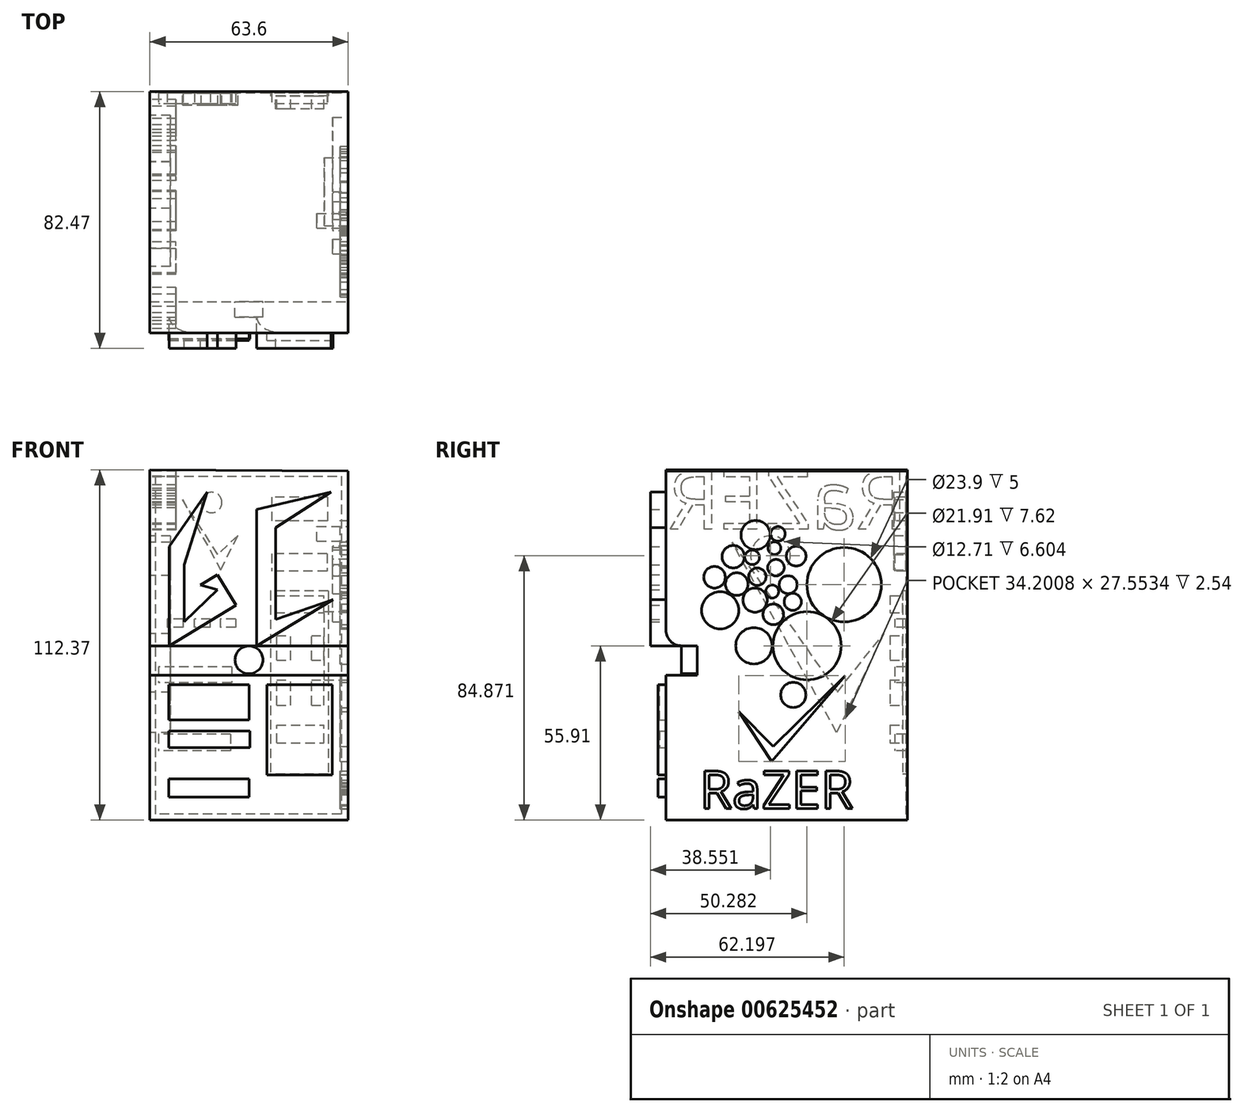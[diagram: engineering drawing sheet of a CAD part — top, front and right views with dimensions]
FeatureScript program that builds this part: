
annotation { "Feature Type Name" : "Feature", "Feature Type Description" : "" }
export const myFeature = defineFeature(function(context is Context, id is Id, definition is map)
    precondition{}
    {
        {
            var Q0;
            Q0=qCreatedBy(makeId("Front.planeOp"),FACE);
            var sketch = newSketch(context, id + "F0", { "sketchPlane" : qUnion([Q0])});
            skLineSegment(sketch, "E0", {"start": v(-45.18, 56.46) * mm, "end": v(-45.18, -55.9) * mm});
            skLineSegment(sketch, "E1", {"start": v(-45.18, -55.9) * mm, "end": v(18.42, -55.9) * mm});
            skLineSegment(sketch, "E2", {"start": v(18.42, -55.9) * mm, "end": v(18.42, 56.09) * mm});
            skLineSegment(sketch, "E3", {"start": v(18.42, 56.09) * mm, "end": v(-45.18, 56.46) * mm});
            skPoint(sketch, "E4.orphan", {"position": v(-43.53, 53.16) * mm});
            skPoint(sketch, "E5.start.orphan", {"position": v(-43.53, 51.7) * mm});
            skSolve(sketch);
        }
        {
            var Q0;
            Q0 = qSketchRegion(id + "F0", true);
            extrude(context, id + "F1", {"entities" : qUnion([Q0]), "depth" : 77.47 * mm, "offsetDistance" : 25.4 * mm});
        }
        {
            var Q0;
            Q0=makeQuery(id+"F1.opExtrude","CAP_FACE",FACE,{"disambiguationData":[OSD([sQuery(id+"F0.wireOp",EDGE,"E0"),sQuery(id+"F0.wireOp",EDGE,"E1"),sQuery(id+"F0.wireOp",EDGE,"E2"),sQuery(id+"F0.wireOp",EDGE,"E3")])],"isStart":false});
            var sketch = newSketch(context, id + "F2", { "sketchPlane" : qUnion([Q0])});
            skLineSegment(sketch, "E6", {"start": v(-26.85, 49.3) * mm, "end": v(-38.95, 31.9) * mm});
            skLineSegment(sketch, "E7", {"start": v(-38.95, 31.9) * mm, "end": v(-38.95, 0) * mm});
            skLineSegment(sketch, "E8", {"start": v(-38.95, 0) * mm, "end": v(-17.5, 13.01) * mm});
            skLineSegment(sketch, "E9", {"start": v(-17.5, 13.01) * mm, "end": v(-23.49, 22.87) * mm});
            skLineSegment(sketch, "E10", {"start": v(-23.49, 22.87) * mm, "end": v(-28.95, 19.56) * mm});
            skLineSegment(sketch, "E11", {"start": v(-28.95, 19.56) * mm, "end": v(-23.49, 17.96) * mm});
            skLineSegment(sketch, "E12", {"start": v(-23.49, 17.96) * mm, "end": v(-34.19, 7.7) * mm});
            skLineSegment(sketch, "E13", {"start": v(-34.19, 7.7) * mm, "end": v(-34.19, 26.03) * mm});
            skLineSegment(sketch, "E14", {"start": v(-34.19, 26.03) * mm, "end": v(-26.85, 49.3) * mm});
            skLineSegment(sketch, "E15", {"start": v(12.92, 49.3) * mm, "end": v(-10.9, 43.8) * mm});
            skLineSegment(sketch, "E16", {"start": v(-10.9, 43.8) * mm, "end": v(-10.9, 0) * mm});
            skLineSegment(sketch, "E17", {"start": v(-10.9, 0) * mm, "end": v(13.57, 14.85) * mm});
            skLineSegment(sketch, "E18", {"start": v(13.57, 14.85) * mm, "end": v(-4.86, 8.43) * mm});
            skLineSegment(sketch, "E19", {"start": v(-4.86, 8.43) * mm, "end": v(-4.86, 37.94) * mm});
            skLineSegment(sketch, "E20", {"start": v(-4.86, 37.94) * mm, "end": v(12.92, 49.3) * mm});
            skSolve(sketch);
        }
        {
            var Q0;
            Q0 = qSketchRegion(id + "F2", true);
            extrude(context, id + "F3", {"entities" : qUnion([Q0]), "operationType" : NewBodyOperationType.ADD, "depth" : 5 * mm, "offsetDistance" : 25.4 * mm});
        }
        {
            var Q0;
            Q0=makeQuery(id+"F1.opExtrude","CAP_FACE",FACE,{"disambiguationData":[OSD([sQuery(id+"F0.wireOp",EDGE,"E0"),sQuery(id+"F0.wireOp",EDGE,"E1"),sQuery(id+"F0.wireOp",EDGE,"E2"),sQuery(id+"F0.wireOp",EDGE,"E3")])],"isStart":false});
            var sketch = newSketch(context, id + "F4", { "sketchPlane" : qUnion([Q0])});
            skLineSegment(sketch, "E21", {"start": v(-39.13, -12.46) * mm, "end": v(-13.29, -12.46) * mm});
            skLineSegment(sketch, "E22", {"start": v(-13.29, -12.46) * mm, "end": v(-13.29, -23.83) * mm});
            skLineSegment(sketch, "E23", {"start": v(-13.29, -23.83) * mm, "end": v(-39.13, -23.83) * mm});
            skLineSegment(sketch, "E24", {"start": v(-39.13, -23.83) * mm, "end": v(-39.13, -12.46) * mm});
            skLineSegment(sketch, "E25", {"start": v(-13.1, -27.31) * mm, "end": v(-13.1, -32.63) * mm});
            skLineSegment(sketch, "E26", {"start": v(-13.1, -32.63) * mm, "end": v(-39.13, -32.63) * mm});
            skLineSegment(sketch, "E27", {"start": v(-39.13, -32.63) * mm, "end": v(-39.13, -27.31) * mm});
            skLineSegment(sketch, "E28", {"start": v(-39.13, -27.31) * mm, "end": v(-13.1, -27.31) * mm});
            skSolve(sketch);
        }
        {
            var Q0;
            Q0 = qSketchRegion(id + "F4", true);
            extrude(context, id + "F5", {"entities" : qUnion([Q0]), "operationType" : NewBodyOperationType.ADD, "depth" : 2 * mm, "offsetDistance" : 25.4 * mm});
        }
        {
            var Q0;
            Q0=makeQuery(id+"F1.opExtrude","SWEPT_FACE",FACE,{"disambiguationData":[OSD([sQuery(id+"F0.wireOp",EDGE,"E2")])]});
            var sketch = newSketch(context, id + "F6", { "sketchPlane" : qUnion([Q0])});
            skCircle(sketch, "E29", {"center": v(-41.54, 35.93) * mm, "radius": 2.35 * mm});
            skSolve(sketch);
        }
        {
            var Q0;
            Q0=makeQuery(id+"F6.imprint","IMPRINT",FACE,{"disambiguationData":[TD([[makeQuery(id+"F6.imprint","IMPRINT",EDGE,{"derivedFrom":sQuery(id+"F6.wireOp",EDGE,"E29")}),1.0]])]});
            extrude(context, id + "F7", {"entities" : qUnion([Q0]), "operationType" : NewBodyOperationType.REMOVE, "oppositeDirection" : true, "depth" : 10 * mm, "offsetDistance" : 25.4 * mm});
        }
        {
            var Q0;
            Q0=makeQuery(id+"F1.opExtrude","SWEPT_FACE",FACE,{"disambiguationData":[OSD([sQuery(id+"F0.wireOp",EDGE,"E2")])]});
            var sketch = newSketch(context, id + "F8", { "sketchPlane" : qUnion([Q0])});
            skCircle(sketch, "E30", {"center": v(-49.78, 28.41) * mm, "radius": 2.35 * mm});
            skSolve(sketch);
        }
        {
            var Q0;
            Q0=makeQuery(id+"F8.imprint","IMPRINT",FACE,{"disambiguationData":[TD([[makeQuery(id+"F8.imprint","IMPRINT",EDGE,{"derivedFrom":sQuery(id+"F8.wireOp",EDGE,"E30")}),1.0]])]});
            extrude(context, id + "F9", {"entities" : qUnion([Q0]), "operationType" : NewBodyOperationType.REMOVE, "endBound" : BoundingType.SYMMETRIC, "oppositeDirection" : true, "depth" : 10 * mm, "offsetDistance" : 25.4 * mm});
        }
        {
            var Q0;
            Q0=makeQuery(id+"F1.opExtrude","SWEPT_FACE",FACE,{"disambiguationData":[OSD([sQuery(id+"F0.wireOp",EDGE,"E2")])]});
            var sketch = newSketch(context, id + "F10", { "sketchPlane" : qUnion([Q0])});
            skCircle(sketch, "E31", {"center": v(-42.16, 25.08) * mm, "radius": 2.64 * mm});
            skSolve(sketch);
        }
        {
            var Q0;
            Q0=makeQuery(id+"F10.imprint","IMPRINT",FACE,{"disambiguationData":[TD([[makeQuery(id+"F10.imprint","IMPRINT",EDGE,{"derivedFrom":sQuery(id+"F10.wireOp",EDGE,"E31")}),1.0]])]});
            extrude(context, id + "F11", {"entities" : qUnion([Q0]), "operationType" : NewBodyOperationType.REMOVE, "endBound" : BoundingType.SYMMETRIC, "depth" : 10 * mm, "offsetDistance" : 25.4 * mm});
        }
        {
            var Q0;
            Q0=makeQuery(id+"F1.opExtrude","SWEPT_FACE",FACE,{"disambiguationData":[OSD([sQuery(id+"F0.wireOp",EDGE,"E2")])]});
            var sketch = newSketch(context, id + "F12", { "sketchPlane" : qUnion([Q0])});
            skCircle(sketch, "E32", {"center": v(-35.67, 28.78) * mm, "radius": 3.14 * mm});
            skSolve(sketch);
        }
        {
            var Q0;
            Q0=makeQuery(id+"F12.imprint","IMPRINT",FACE,{"disambiguationData":[TD([[makeQuery(id+"F12.imprint","IMPRINT",EDGE,{"derivedFrom":sQuery(id+"F12.wireOp",EDGE,"E32")}),1.0]])]});
            extrude(context, id + "F13", {"entities" : qUnion([Q0]), "operationType" : NewBodyOperationType.REMOVE, "endBound" : BoundingType.SYMMETRIC, "depth" : 10 * mm, "offsetDistance" : 25.4 * mm});
        }
        {
            var Q0;
            Q0=makeQuery(id+"F1.opExtrude","SWEPT_FACE",FACE,{"disambiguationData":[OSD([sQuery(id+"F0.wireOp",EDGE,"E2")])]});
            var sketch = newSketch(context, id + "F14", { "sketchPlane" : qUnion([Q0])});
            skCircle(sketch, "E33", {"center": v(-38.24, 19.61) * mm, "radius": 2.87 * mm});
            skSolve(sketch);
        }
        {
            var Q0;
            Q0=makeQuery(id+"F14.imprint","IMPRINT",FACE,{"disambiguationData":[TD([[makeQuery(id+"F14.imprint","IMPRINT",EDGE,{"derivedFrom":sQuery(id+"F14.wireOp",EDGE,"E33")}),1.0]])]});
            extrude(context, id + "F15", {"entities" : qUnion([Q0]), "operationType" : NewBodyOperationType.REMOVE, "endBound" : BoundingType.SYMMETRIC, "oppositeDirection" : true, "depth" : 10 * mm, "offsetDistance" : 25.4 * mm});
        }
        {
            var Q0;
            Q0=makeQuery(id+"F1.opExtrude","SWEPT_FACE",FACE,{"disambiguationData":[OSD([sQuery(id+"F0.wireOp",EDGE,"E2")])]});
            var sketch = newSketch(context, id + "F16", { "sketchPlane" : qUnion([Q0])});
            skCircle(sketch, "E34", {"center": v(-20.27, 19.61) * mm, "radius": 11.95 * mm});
            skSolve(sketch);
        }
        {
            var Q0;
            Q0=makeQuery(id+"F16.imprint","IMPRINT",FACE,{"disambiguationData":[TD([[makeQuery(id+"F16.imprint","IMPRINT",EDGE,{"derivedFrom":sQuery(id+"F16.wireOp",EDGE,"E34")}),1.0]])]});
            extrude(context, id + "F17", {"entities" : qUnion([Q0]), "operationType" : NewBodyOperationType.REMOVE, "endBound" : BoundingType.SYMMETRIC, "oppositeDirection" : true, "depth" : 10 * mm, "offsetDistance" : 25.4 * mm});
        }
        {
            var Q0;
            Q0=makeQuery(id+"F1.opExtrude","SWEPT_FACE",FACE,{"disambiguationData":[OSD([sQuery(id+"F0.wireOp",EDGE,"E2")])]});
            var sketch = newSketch(context, id + "F18", { "sketchPlane" : qUnion([Q0])});
            skCircle(sketch, "E35", {"center": v(-32.19, 0) * mm, "radius": 10.96 * mm});
            skSolve(sketch);
        }
        {
            var Q0;
            Q0=makeQuery(id+"F18.imprint","IMPRINT",FACE,{"disambiguationData":[TD([[makeQuery(id+"F18.imprint","IMPRINT",EDGE,{"derivedFrom":sQuery(id+"F18.wireOp",EDGE,"E35")}),1.0]])]});
            extrude(context, id + "F19", {"entities" : qUnion([Q0]), "operationType" : NewBodyOperationType.REMOVE, "endBound" : BoundingType.SYMMETRIC, "oppositeDirection" : true, "depth" : 15.24 * mm, "offsetDistance" : 25.4 * mm});
        }
        {
            var Q0;
            Q0=makeQuery(id+"F0.imprint","IMPRINT",FACE,{"disambiguationData":[TD([[makeQuery(id+"F0.imprint","IMPRINT",EDGE,{"derivedFrom":sQuery(id+"F0.wireOp",EDGE,"E0")}),1.0]])]});
            var sketch = newSketch(context, id + "F20", { "sketchPlane" : qUnion([Q0])});
            skLineSegment(sketch, "E36", {"start": v(16.22, 54.44) * mm, "end": v(16.22, -54.07) * mm});
            skLineSegment(sketch, "E37", {"start": v(16.22, -54.07) * mm, "end": v(-43.35, -54.07) * mm});
            skLineSegment(sketch, "E38", {"start": v(-43.35, -54.07) * mm, "end": v(-43.35, 54.44) * mm});
            skLineSegment(sketch, "E39", {"start": v(-43.35, 54.44) * mm, "end": v(16.22, 54.44) * mm});
            skSolve(sketch);
        }
        {
            var Q0;
            Q0 = qSketchRegion(id + "F20", true);
            extrude(context, id + "F21", {"entities" : qUnion([Q0]), "operationType" : NewBodyOperationType.REMOVE, "endBound" : BoundingType.SYMMETRIC, "oppositeDirection" : true, "depth" : 1 * mm, "offsetDistance" : 25.4 * mm});
        }
        {
            var Q0;
            Q0=makeQuery(id+"F0.imprint","IMPRINT",FACE,{"disambiguationData":[TD([[makeQuery(id+"F0.imprint","IMPRINT",EDGE,{"derivedFrom":sQuery(id+"F0.wireOp",EDGE,"E0")}),1.0]])]});
            var sketch = newSketch(context, id + "F22", { "sketchPlane" : qUnion([Q0])});
            skLineSegment(sketch, "E40.bottom", {"start": v(11.82, 47.66) * mm, "end": v(-6.14, 47.66) * mm});
            skLineSegment(sketch, "E40.top", {"start": v(11.82, 40.14) * mm, "end": v(-6.14, 40.14) * mm});
            skLineSegment(sketch, "E40.left", {"start": v(11.82, 47.66) * mm, "end": v(11.82, 40.14) * mm});
            skLineSegment(sketch, "E40.right", {"start": v(-6.14, 47.66) * mm, "end": v(-6.14, 40.14) * mm});
            skLineSegment(sketch, "E41.bottom", {"start": v(11.64, 29.51) * mm, "end": v(-6.14, 29.51) * mm});
            skLineSegment(sketch, "E41.top", {"start": v(11.64, 24.01) * mm, "end": v(-6.14, 24.01) * mm});
            skLineSegment(sketch, "E41.left", {"start": v(11.64, 29.51) * mm, "end": v(11.64, 24.01) * mm});
            skLineSegment(sketch, "E41.right", {"start": v(-6.14, 29.51) * mm, "end": v(-6.14, 24.01) * mm});
            skLineSegment(sketch, "E42.bottom", {"start": v(-17.69, 8.62) * mm, "end": v(-22.64, 8.62) * mm});
            skLineSegment(sketch, "E42.top", {"start": v(-17.69, 5.87) * mm, "end": v(-22.64, 5.87) * mm});
            skLineSegment(sketch, "E42.left", {"start": v(-17.69, 8.62) * mm, "end": v(-17.69, 5.87) * mm});
            skLineSegment(sketch, "E42.right", {"start": v(-22.64, 8.62) * mm, "end": v(-22.64, 5.87) * mm});
            skLineSegment(sketch, "E43.bottom", {"start": v(-18.97, -6.78) * mm, "end": v(-42.43, -6.78) * mm});
            skLineSegment(sketch, "E43.top", {"start": v(-18.97, -11.91) * mm, "end": v(-42.43, -11.91) * mm});
            skLineSegment(sketch, "E43.left", {"start": v(-18.97, -6.78) * mm, "end": v(-18.97, -11.91) * mm});
            skLineSegment(sketch, "E43.right", {"start": v(-42.43, -6.78) * mm, "end": v(-42.43, -11.91) * mm});
            skLineSegment(sketch, "E44.bottom", {"start": v(-19.34, -28.41) * mm, "end": v(-42.43, -28.41) * mm});
            skLineSegment(sketch, "E44.top", {"start": v(-19.34, -33.73) * mm, "end": v(-42.43, -33.73) * mm});
            skLineSegment(sketch, "E44.left", {"start": v(-19.34, -28.41) * mm, "end": v(-19.34, -33.73) * mm});
            skLineSegment(sketch, "E44.right", {"start": v(-42.43, -28.41) * mm, "end": v(-42.43, -33.73) * mm});
            skLineSegment(sketch, "E45.bottom", {"start": v(-25.75, 5.87) * mm, "end": v(-30.89, 5.87) * mm});
            skLineSegment(sketch, "E45.top", {"start": v(-25.75, 8.62) * mm, "end": v(-30.89, 8.62) * mm});
            skLineSegment(sketch, "E45.left", {"start": v(-25.75, 5.87) * mm, "end": v(-25.75, 8.62) * mm});
            skLineSegment(sketch, "E45.right", {"start": v(-30.89, 5.87) * mm, "end": v(-30.89, 8.62) * mm});
            skLineSegment(sketch, "E46.bottom", {"start": v(-34.55, 8.62) * mm, "end": v(-39.68, 8.62) * mm});
            skLineSegment(sketch, "E46.top", {"start": v(-34.55, 5.87) * mm, "end": v(-39.68, 5.87) * mm});
            skLineSegment(sketch, "E46.left", {"start": v(-34.55, 8.62) * mm, "end": v(-34.55, 5.87) * mm});
            skLineSegment(sketch, "E46.right", {"start": v(-39.68, 8.62) * mm, "end": v(-39.68, 5.87) * mm});
            skSolve(sketch);
        }
        {
            var Q0;
            Q0 = qSketchRegion(id + "F22", true);
            extrude(context, id + "F23", {"entities" : qUnion([Q0]), "operationType" : NewBodyOperationType.REMOVE, "endBound" : BoundingType.SYMMETRIC, "oppositeDirection" : true, "depth" : 8 * mm, "offsetDistance" : 25.4 * mm});
        }
        {
            var Q0;
            Q0=makeQuery(id+"F1.opExtrude","SWEPT_FACE",FACE,{"disambiguationData":[OSD([sQuery(id+"F0.wireOp",EDGE,"E0")])]});
            var sketch = newSketch(context, id + "F24", { "sketchPlane" : qUnion([Q0])});
            skText(sketch, "E47", { "text": "RaZER\n", "fontName": "OpenSans-Regular.ttf"});
            const initialGuessF24  = {"E47": [0, 0.03739, 1, 0, 0.01888]};
            skSetInitialGuess(sketch, initialGuessF24);
            skSolve(sketch);
        }
        {
            var Q0;
            Q0 = qSketchRegion(id + "F24", true);
            extrude(context, id + "F25", {"entities" : qUnion([Q0]), "operationType" : NewBodyOperationType.REMOVE, "endBound" : BoundingType.SYMMETRIC, "oppositeDirection" : true, "depth" : 16.76 * mm, "offsetDistance" : 25.4 * mm});
        }
        {
            var Q0;
            {var subQ2=sQuery(id+"F0.wireOp",EDGE,"E1");var subQ3=sQuery(id+"F0.wireOp",EDGE,"E0");Q0=makeQuery(id+"F25.boolean.opBoolean","SPLIT",FACE,{"disambiguationData":[TD([makeQuery(id+"F1.opExtrude","SWEPT_FACE",FACE,{"disambiguationData":[OSD([subQ2])]})])],"derivedFrom":makeQuery(id+"F1.opExtrude","SWEPT_FACE",FACE,{"disambiguationData":[OSD([subQ3])]})});}
            var sketch = newSketch(context, id + "F26", { "sketchPlane" : qUnion([Q0])});
            skLineSegment(sketch, "E48", {"start": v(56.2, 33.18) * mm, "end": v(22.47, -14.85) * mm});
            skLineSegment(sketch, "E49", {"start": v(22.47, -14.85) * mm, "end": v(7.63, 3.85) * mm});
            skLineSegment(sketch, "E50", {"start": v(7.63, 3.85) * mm, "end": v(22.66, -27.86) * mm});
            skLineSegment(sketch, "E51", {"start": v(22.66, -27.86) * mm, "end": v(56.2, 33.18) * mm});
            skCircle(sketch, "E52", {"center": v(43.92, 28.96) * mm, "radius": 6.35 * mm});
            skSolve(sketch);
        }
        {
            var Q0;
            Q0=makeQuery(id+"F26.imprint","IMPRINT",FACE,{"disambiguationData":[TD([[makeQuery(id+"F26.imprint","IMPRINT",EDGE,{"derivedFrom":sQuery(id+"F26.wireOp",EDGE,"E52")}),1.0]])]});
            var Q1;
            Q1=makeQuery(id+"F26.imprint","IMPRINT",FACE,{"disambiguationData":[TD([[makeQuery(id+"F26.imprint","IMPRINT",EDGE,{"derivedFrom":sQuery(id+"F26.wireOp",EDGE,"E48")}),1.0]])]});
            extrude(context, id + "F27", {"entities" : qUnion([Q0, Q1]), "operationType" : NewBodyOperationType.REMOVE, "oppositeDirection" : true, "depth" : 6.6 * mm, "offsetDistance" : 25.4 * mm});
        }
        {
            var Q0;
            Q0=makeQuery(id+"F1.opExtrude","CAP_FACE",FACE,{"disambiguationData":[OSD([sQuery(id+"F0.wireOp",EDGE,"E0"),sQuery(id+"F0.wireOp",EDGE,"E1"),sQuery(id+"F0.wireOp",EDGE,"E2"),sQuery(id+"F0.wireOp",EDGE,"E3")])],"isStart":false});
            var sketch = newSketch(context, id + "F28", { "sketchPlane" : qUnion([Q0])});
            skPoint(sketch, "E53.firstSnap0", {"position": v(-39.13, -29.97) * mm});
            skLineSegment(sketch, "E53.bottom", {"start": v(-39.13, -42.7) * mm, "end": v(-13.29, -42.7) * mm});
            skLineSegment(sketch, "E53.top", {"start": v(-39.13, -48.57) * mm, "end": v(-13.29, -48.57) * mm});
            skLineSegment(sketch, "E53.left", {"start": v(-39.13, -42.7) * mm, "end": v(-39.13, -48.57) * mm});
            skLineSegment(sketch, "E53.right", {"start": v(-13.29, -42.7) * mm, "end": v(-13.29, -48.57) * mm});
            skLineSegment(sketch, "E54.bottom", {"start": v(-7.6, -41.43) * mm, "end": v(13.29, -41.43) * mm});
            skLineSegment(sketch, "E54.top", {"start": v(-7.6, -12.46) * mm, "end": v(13.29, -12.46) * mm});
            skLineSegment(sketch, "E54.left", {"start": v(-7.6, -41.43) * mm, "end": v(-7.6, -12.46) * mm});
            skLineSegment(sketch, "E54.right", {"start": v(13.29, -41.43) * mm, "end": v(13.29, -12.46) * mm});
            skSolve(sketch);
        }
        {
            var Q0;
            Q0 = qSketchRegion(id + "F28", true);
            extrude(context, id + "F29", {"entities" : qUnion([Q0]), "operationType" : NewBodyOperationType.ADD, "depth" : 2.5 * mm, "offsetDistance" : 25.4 * mm});
        }
        {
            var Q0;
            Q0=makeQuery(id+"F1.opExtrude","SWEPT_FACE",FACE,{"disambiguationData":[OSD([sQuery(id+"F0.wireOp",EDGE,"E2")])]});
            var sketch = newSketch(context, id + "F30", { "sketchPlane" : qUnion([Q0])});
            skCircle(sketch, "E55", {"center": v(-54.73, 19.8) * mm, "radius": 3.64 * mm});
            skCircle(sketch, "E56", {"center": v(-48.87, 14.66) * mm, "radius": 3.89 * mm});
            skCircle(sketch, "E57", {"center": v(-43, 10.08) * mm, "radius": 3.3 * mm});
            skCircle(sketch, "E58", {"center": v(-42.64, 31.34) * mm, "radius": 2.05 * mm});
            skCircle(sketch, "E59", {"center": v(-48.13, 22.18) * mm, "radius": 2.8 * mm});
            skCircle(sketch, "E60", {"center": v(-43.37, 17.41) * mm, "radius": 2.09 * mm});
            skCircle(sketch, "E61", {"center": v(-49.23, 0) * mm, "radius": 5.83 * mm});
            skCircle(sketch, "E62", {"center": v(-60.05, 11.36) * mm, "radius": 5.97 * mm});
            skCircle(sketch, "E63", {"center": v(-36.77, 14.11) * mm, "radius": 2.75 * mm});
            skCircle(sketch, "E64", {"center": v(-48.68, 35.56) * mm, "radius": 4.68 * mm});
            skCircle(sketch, "E65", {"center": v(-55.83, 28.6) * mm, "radius": 3.6 * mm});
            skCircle(sketch, "E66", {"center": v(-61.88, 22) * mm, "radius": 3.46 * mm});
            skSolve(sketch);
        }
        {
            var Q0;
            Q0 = qSketchRegion(id + "F30", true);
            extrude(context, id + "F31", {"entities" : qUnion([Q0]), "operationType" : NewBodyOperationType.REMOVE, "endBound" : BoundingType.SYMMETRIC, "oppositeDirection" : true, "depth" : 5 * mm, "offsetDistance" : 25.4 * mm});
        }
        {
            var Q0;
            Q0=makeQuery(id+"F0.imprint","IMPRINT",FACE,{"disambiguationData":[TD([[makeQuery(id+"F0.imprint","IMPRINT",EDGE,{"derivedFrom":sQuery(id+"F0.wireOp",EDGE,"E0")}),1.0]])]});
            var sketch = newSketch(context, id + "F32", { "sketchPlane" : qUnion([Q0])});
            skLineSegment(sketch, "E67.bottom", {"start": v(12, 17.6) * mm, "end": v(-6.5, 17.6) * mm});
            skLineSegment(sketch, "E67.top", {"start": v(12, -41.24) * mm, "end": v(-6.5, -41.24) * mm});
            skLineSegment(sketch, "E67.left", {"start": v(12, 17.6) * mm, "end": v(12, -41.24) * mm});
            skLineSegment(sketch, "E67.right", {"start": v(-6.5, 17.6) * mm, "end": v(-6.5, -41.24) * mm});
            skSolve(sketch);
        }
        {
            var Q0;
            Q0 = qSketchRegion(id + "F32", true);
            extrude(context, id + "F33", {"entities" : qUnion([Q0]), "operationType" : NewBodyOperationType.REMOVE, "endBound" : BoundingType.SYMMETRIC, "oppositeDirection" : true, "depth" : 3 * mm, "offsetDistance" : 25.4 * mm});
        }
        {
            var Q0;
            Q0=makeQuery(id+"F0.imprint","IMPRINT",FACE,{"disambiguationData":[TD([[makeQuery(id+"F0.imprint","IMPRINT",EDGE,{"derivedFrom":sQuery(id+"F0.wireOp",EDGE,"E0")}),1.0]])]});
            var sketch = newSketch(context, id + "F34", { "sketchPlane" : qUnion([Q0])});
            skLineSegment(sketch, "E68.bottom", {"start": v(10.72, 16.13) * mm, "end": v(-4.86, 16.13) * mm});
            skLineSegment(sketch, "E68.top", {"start": v(10.72, 10.63) * mm, "end": v(-4.86, 10.63) * mm});
            skLineSegment(sketch, "E68.left", {"start": v(10.72, 16.13) * mm, "end": v(10.72, 10.63) * mm});
            skLineSegment(sketch, "E68.right", {"start": v(-4.86, 16.13) * mm, "end": v(-4.86, 10.63) * mm});
            skLineSegment(sketch, "E69.bottom", {"start": v(10.72, 3.3) * mm, "end": v(6.7, 3.3) * mm});
            skLineSegment(sketch, "E69.top", {"start": v(10.72, -4.58) * mm, "end": v(6.7, -4.58) * mm});
            skLineSegment(sketch, "E69.left", {"start": v(10.72, 3.3) * mm, "end": v(10.72, -4.58) * mm});
            skLineSegment(sketch, "E69.right", {"start": v(6.7, 3.3) * mm, "end": v(6.7, -4.58) * mm});
            skLineSegment(sketch, "E70.bottom", {"start": v(10.72, -11) * mm, "end": v(6.7, -11) * mm});
            skLineSegment(sketch, "E70.top", {"start": v(10.72, -19.06) * mm, "end": v(6.7, -19.06) * mm});
            skLineSegment(sketch, "E70.left", {"start": v(10.72, -11) * mm, "end": v(10.72, -19.06) * mm});
            skLineSegment(sketch, "E70.right", {"start": v(6.7, -11) * mm, "end": v(6.7, -19.06) * mm});
            skLineSegment(sketch, "E71.bottom", {"start": v(0, 3.3) * mm, "end": v(-4.5, 3.3) * mm});
            skLineSegment(sketch, "E71.top", {"start": v(0, -4.58) * mm, "end": v(-4.5, -4.58) * mm});
            skLineSegment(sketch, "E71.left", {"start": v(0, 3.3) * mm, "end": v(0, -4.58) * mm});
            skLineSegment(sketch, "E71.right", {"start": v(-4.5, 3.3) * mm, "end": v(-4.5, -4.58) * mm});
            skLineSegment(sketch, "E72.bottom", {"start": v(0, -11) * mm, "end": v(-4.5, -11) * mm});
            skLineSegment(sketch, "E72.top", {"start": v(0, -19.06) * mm, "end": v(-4.5, -19.06) * mm});
            skLineSegment(sketch, "E72.left", {"start": v(0, -11) * mm, "end": v(0, -19.06) * mm});
            skLineSegment(sketch, "E72.right", {"start": v(-4.5, -11) * mm, "end": v(-4.5, -19.06) * mm});
            skLineSegment(sketch, "E73.bottom", {"start": v(10.72, -25.48) * mm, "end": v(-4.5, -25.48) * mm});
            skLineSegment(sketch, "E73.top", {"start": v(10.72, -31.16) * mm, "end": v(-4.5, -31.16) * mm});
            skLineSegment(sketch, "E73.left", {"start": v(10.72, -25.48) * mm, "end": v(10.72, -31.16) * mm});
            skLineSegment(sketch, "E73.right", {"start": v(-4.5, -25.48) * mm, "end": v(-4.5, -31.16) * mm});
            skSolve(sketch);
        }
        {
            var Q0;
            Q0 = qSketchRegion(id + "F34", true);
            extrude(context, id + "F35", {"entities" : qUnion([Q0]), "operationType" : NewBodyOperationType.REMOVE, "endBound" : BoundingType.SYMMETRIC, "depth" : 11.18 * mm, "offsetDistance" : 25.4 * mm});
        }
        {
            var Q0;
            Q0=makeQuery(id+"F0.imprint","IMPRINT",FACE,{"disambiguationData":[TD([[makeQuery(id+"F0.imprint","IMPRINT",EDGE,{"derivedFrom":sQuery(id+"F0.wireOp",EDGE,"E0")}),1.0]])]});
            var sketch = newSketch(context, id + "F36", { "sketchPlane" : qUnion([Q0])});
            skCircle(sketch, "E74", {"center": v(-25.39, 46) * mm, "radius": 3.3 * mm});
            skLineSegment(sketch, "E75", {"start": v(-34.74, 46.92) * mm, "end": v(-23.37, 29.33) * mm});
            skLineSegment(sketch, "E76", {"start": v(-23.37, 29.33) * mm, "end": v(-16.96, 35.38) * mm});
            skLineSegment(sketch, "E77", {"start": v(-16.96, 35.38) * mm, "end": v(-22.45, 24.38) * mm});
            skLineSegment(sketch, "E78", {"start": v(-22.45, 24.38) * mm, "end": v(-34.74, 46.92) * mm});
            skSolve(sketch);
        }
        {
            var Q0;
            Q0 = qSketchRegion(id + "F36", true);
            extrude(context, id + "F37", {"entities" : qUnion([Q0]), "operationType" : NewBodyOperationType.REMOVE, "depth" : 4.32 * mm, "offsetDistance" : 25.4 * mm});
        }
        {
            var Q0;
            Q0=makeQuery(id+"F1.opExtrude","CAP_FACE",FACE,{"disambiguationData":[OSD([sQuery(id+"F0.wireOp",EDGE,"E0"),sQuery(id+"F0.wireOp",EDGE,"E1"),sQuery(id+"F0.wireOp",EDGE,"E2"),sQuery(id+"F0.wireOp",EDGE,"E3")])],"isStart":false});
            var sketch = newSketch(context, id + "F38", { "sketchPlane" : qUnion([Q0])});
            skPoint(sketch, "E79.firstSnap0", {"position": v(-45.18, 0.27) * mm});
            skLineSegment(sketch, "E79.bottom", {"start": v(-45.18, 0) * mm, "end": v(18.42, 0) * mm});
            skLineSegment(sketch, "E79.top", {"start": v(-45.18, -9.5) * mm, "end": v(18.42, -9.5) * mm});
            skLineSegment(sketch, "E79.left", {"start": v(-45.18, 0) * mm, "end": v(-45.18, -9.5) * mm});
            skLineSegment(sketch, "E79.right", {"start": v(18.42, 0) * mm, "end": v(18.42, -9.5) * mm});
            skSolve(sketch);
        }
        {
            var Q0;
            Q0 = qSketchRegion(id + "F38", true);
            extrude(context, id + "F39", {"entities" : qUnion([Q0]), "operationType" : NewBodyOperationType.REMOVE, "oppositeDirection" : true, "depth" : 10 * mm, "offsetDistance" : 25.4 * mm});
        }
        {
            var Q0;
            {var subQ0=sQuery(id+"F38.wireOp",EDGE,"E79.bottom");Q0=makeQuery(id+"F39.boolean.opBoolean","COPY",EDGE,{"disambiguationData":[TD([makeQuery(id+"F1.opExtrude","CAP_FACE",FACE,{"disambiguationData":[OSD([sQuery(id+"F0.wireOp",EDGE,"E0"),sQuery(id+"F0.wireOp",EDGE,"E1"),sQuery(id+"F0.wireOp",EDGE,"E2"),sQuery(id+"F0.wireOp",EDGE,"E3")])],"isStart":false}),makeQuery(id+"F3.opExtrude","SWEPT_FACE",FACE,{"disambiguationData":[OSD([sQuery(id+"F2.wireOp",EDGE,"E7")])]}),makeQuery(id+"F3.opExtrude","SWEPT_FACE",FACE,{"disambiguationData":[OSD([sQuery(id+"F2.wireOp",EDGE,"E8")])]}),makeQuery(id+"F3.opExtrude","SWEPT_FACE",FACE,{"disambiguationData":[OSD([sQuery(id+"F2.wireOp",EDGE,"E16")])]}),makeQuery(id+"F3.opExtrude","SWEPT_FACE",FACE,{"disambiguationData":[OSD([sQuery(id+"F2.wireOp",EDGE,"E17")])]}),makeQuery(id+"F39.opExtrude","SWEPT_FACE",FACE,{"disambiguationData":[OSD([subQ0])]})])],"derivedFrom":makeQuery(id+"F39.opExtrude","CAP_EDGE",EDGE,{"disambiguationData":[OSD([subQ0])],"isStart":true})});}
            var Q1;
            {var subQ0=sQuery(id+"F0.wireOp",EDGE,"E0");var subQ1=sQuery(id+"F38.wireOp",EDGE,"E79.bottom");Q1=makeQuery(id+"F39.boolean.opBoolean","COPY",EDGE,{"disambiguationData":[TD([makeQuery(id+"F1.opExtrude","SWEPT_FACE",FACE,{"disambiguationData":[OSD([subQ0])]}),makeQuery(id+"F1.opExtrude","CAP_FACE",FACE,{"disambiguationData":[OSD([subQ0,sQuery(id+"F0.wireOp",EDGE,"E1"),sQuery(id+"F0.wireOp",EDGE,"E2"),sQuery(id+"F0.wireOp",EDGE,"E3")])],"isStart":false}),makeQuery(id+"F3.opExtrude","SWEPT_FACE",FACE,{"disambiguationData":[OSD([sQuery(id+"F2.wireOp",EDGE,"E7")])]}),makeQuery(id+"F3.opExtrude","SWEPT_FACE",FACE,{"disambiguationData":[OSD([sQuery(id+"F2.wireOp",EDGE,"E8")])]}),makeQuery(id+"F39.opExtrude","SWEPT_FACE",FACE,{"disambiguationData":[OSD([subQ1])]})])],"derivedFrom":makeQuery(id+"F39.opExtrude","CAP_EDGE",EDGE,{"disambiguationData":[OSD([subQ1])],"isStart":true})});}
            var Q2;
            {var subQ0=sQuery(id+"F0.wireOp",EDGE,"E2");var subQ1=sQuery(id+"F38.wireOp",EDGE,"E79.bottom");Q2=makeQuery(id+"F39.boolean.opBoolean","COPY",EDGE,{"disambiguationData":[TD([makeQuery(id+"F1.opExtrude","CAP_FACE",FACE,{"disambiguationData":[OSD([sQuery(id+"F0.wireOp",EDGE,"E0"),sQuery(id+"F0.wireOp",EDGE,"E1"),subQ0,sQuery(id+"F0.wireOp",EDGE,"E3")])],"isStart":false}),makeQuery(id+"F1.opExtrude","SWEPT_FACE",FACE,{"disambiguationData":[OSD([subQ0])]}),makeQuery(id+"F3.opExtrude","SWEPT_FACE",FACE,{"disambiguationData":[OSD([sQuery(id+"F2.wireOp",EDGE,"E16")])]}),makeQuery(id+"F3.opExtrude","SWEPT_FACE",FACE,{"disambiguationData":[OSD([sQuery(id+"F2.wireOp",EDGE,"E17")])]}),makeQuery(id+"F39.opExtrude","SWEPT_FACE",FACE,{"disambiguationData":[OSD([subQ1])]})])],"derivedFrom":makeQuery(id+"F39.opExtrude","CAP_EDGE",EDGE,{"disambiguationData":[OSD([subQ1])],"isStart":true})});}
            var Q3;
            Q3=makeQuery(id+"F39.boolean.opBoolean","COPY",EDGE,{"derivedFrom":makeQuery(id+"F39.opExtrude","CAP_EDGE",EDGE,{"disambiguationData":[OSD([sQuery(id+"F38.wireOp",EDGE,"E79.top")])],"isStart":true})});
            fillet(context, id + "F40", {"entities" : qUnion([Q0, Q1, Q2, Q3]), "radius" : 5.08 * mm, "tangentPropagation" : true, "allowEdgeOverflow" : false});
        }
        {
            var Q0;
            Q0=makeQuery(id+"F39.boolean.opBoolean","COPY",FACE,{"derivedFrom":makeQuery(id+"F39.opExtrude","CAP_FACE",FACE,{"disambiguationData":[OSD([sQuery(id+"F38.wireOp",EDGE,"E79.bottom"),sQuery(id+"F38.wireOp",EDGE,"E79.top"),sQuery(id+"F38.wireOp",EDGE,"E79.left"),sQuery(id+"F38.wireOp",EDGE,"E79.right")])],"isStart":false})});
            var sketch = newSketch(context, id + "F41", { "sketchPlane" : qUnion([Q0])});
            skCircle(sketch, "E80", {"center": v(-13.38, -4.52) * mm, "radius": 4.47 * mm});
            skPoint(sketch, "E80.centerSnap0", {"position": v(-13.38, 0) * mm});
            skSolve(sketch);
        }
        {
            var Q0;
            Q0 = qSketchRegion(id + "F41", true);
            extrude(context, id + "F42", {"entities" : qUnion([Q0]), "operationType" : NewBodyOperationType.ADD, "depth" : 5 * mm, "offsetDistance" : 25.4 * mm});
        }
        {
            var Q0;
            Q0=makeQuery(id+"F1.opExtrude","SWEPT_FACE",FACE,{"disambiguationData":[OSD([sQuery(id+"F0.wireOp",EDGE,"E2")])]});
            var sketch = newSketch(context, id + "F43", { "sketchPlane" : qUnion([Q0])});
            skLineSegment(sketch, "E81", {"start": v(-54.1, -21.1) * mm, "end": v(-43.05, -32.35) * mm});
            skLineSegment(sketch, "E82", {"start": v(-43.05, -32.35) * mm, "end": v(-19.9, -9.6) * mm});
            skLineSegment(sketch, "E83", {"start": v(-19.9, -9.6) * mm, "end": v(-43.6, -37.15) * mm});
            skLineSegment(sketch, "E84", {"start": v(-43.6, -37.15) * mm, "end": v(-54.1, -21.1) * mm});
            skCircle(sketch, "E85", {"center": v(-36.6, -15.76) * mm, "radius": 4.04 * mm});
            skSolve(sketch);
        }
        {
            var Q0;
            Q0 = qSketchRegion(id + "F43", true);
            extrude(context, id + "F44", {"entities" : qUnion([Q0]), "operationType" : NewBodyOperationType.REMOVE, "endBound" : BoundingType.SYMMETRIC, "oppositeDirection" : true, "depth" : 5.08 * mm, "offsetDistance" : 25.4 * mm});
        }
        {
            var Q0;
            Q0=makeQuery(id+"F1.opExtrude","SWEPT_FACE",FACE,{"disambiguationData":[OSD([sQuery(id+"F0.wireOp",EDGE,"E2")])]});
            var sketch = newSketch(context, id + "F45", { "sketchPlane" : qUnion([Q0])});
            skText(sketch, "E86", { "text": "RaZER", "fontName": "OpenSans-Regular.ttf"});
            const initialGuessF45  = {"E86": [-0.06665, -0.05226, 1, 0, 0.01217]};
            skSetInitialGuess(sketch, initialGuessF45);
            skSolve(sketch);
        }
        {
            var Q0;
            Q0 = qSketchRegion(id + "F45", true);
            var Q1;
            Q1 = qConstructionFilter(qBodyType(qCreatedBy(id + "F45" ,EDGE), BodyType.WIRE), ConstructionObject.NO);
            extrude(context, id + "F46", {"entities" : qUnion([Q0]), "operationType" : NewBodyOperationType.REMOVE, "surfaceEntities" : qUnion([Q1]), "endBound" : BoundingType.SYMMETRIC, "oppositeDirection" : true, "depth" : 5 * mm, "offsetDistance" : 25.4 * mm});
        }
    });
